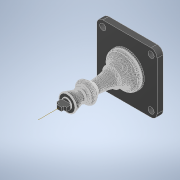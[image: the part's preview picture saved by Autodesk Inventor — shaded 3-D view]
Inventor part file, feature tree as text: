
AUTODESK INVENTOR PART (.ipt)
format: ipt  version: 2022 (Build 260153000, 153)  size: 13,076,992 bytes
history: native  units: mm
features: other x5, sketch x2, move_body x1, extrude x1, chamfer x1, revolve x1, projected_geometry x1
ambient origin geometry x8: Origin, YZ Plane, XZ Plane, XY Plane, X Axis, Y Axis, Z Axis, Center Point
bodies: Solid2 (feature_tree), Solid3 (feature_tree), Solid1 (feature_tree)
feature tree (12):
  other  "Queen Mold.ipt"
  other  "MeshFeature1"
  move_body  "Move Body1"
  extrude  "Extrusion1"  [1 undecoded]
  chamfer  "Chamfer1"  Distance=4.0mm
  revolve  "Revolution1"  Angle=45.0deg
  other  "Solid2::Queen Mold.ipt"
  other  "TaggingFeature1"
  other  "Work Axis1"
  sketch  "Sketch1"  dims[d0=10.0mm d1=-120.755mm d2=-92.942mm d3=-32.396144mm d4=4.0mm d5=0.0mm]
  projected_geometry  "Projected Loop1"
  sketch  "Sketch2"  dims[d6=1.0mm d7=2.0mm d8=45.0deg d9=45.0deg d10=45.0deg d11=90.0deg]
note: 1 required parameter value undecoded (feature->parameter linkage not recoverable at this tier; creation-order binding heuristic only, values carry confidence <= 0.55)
